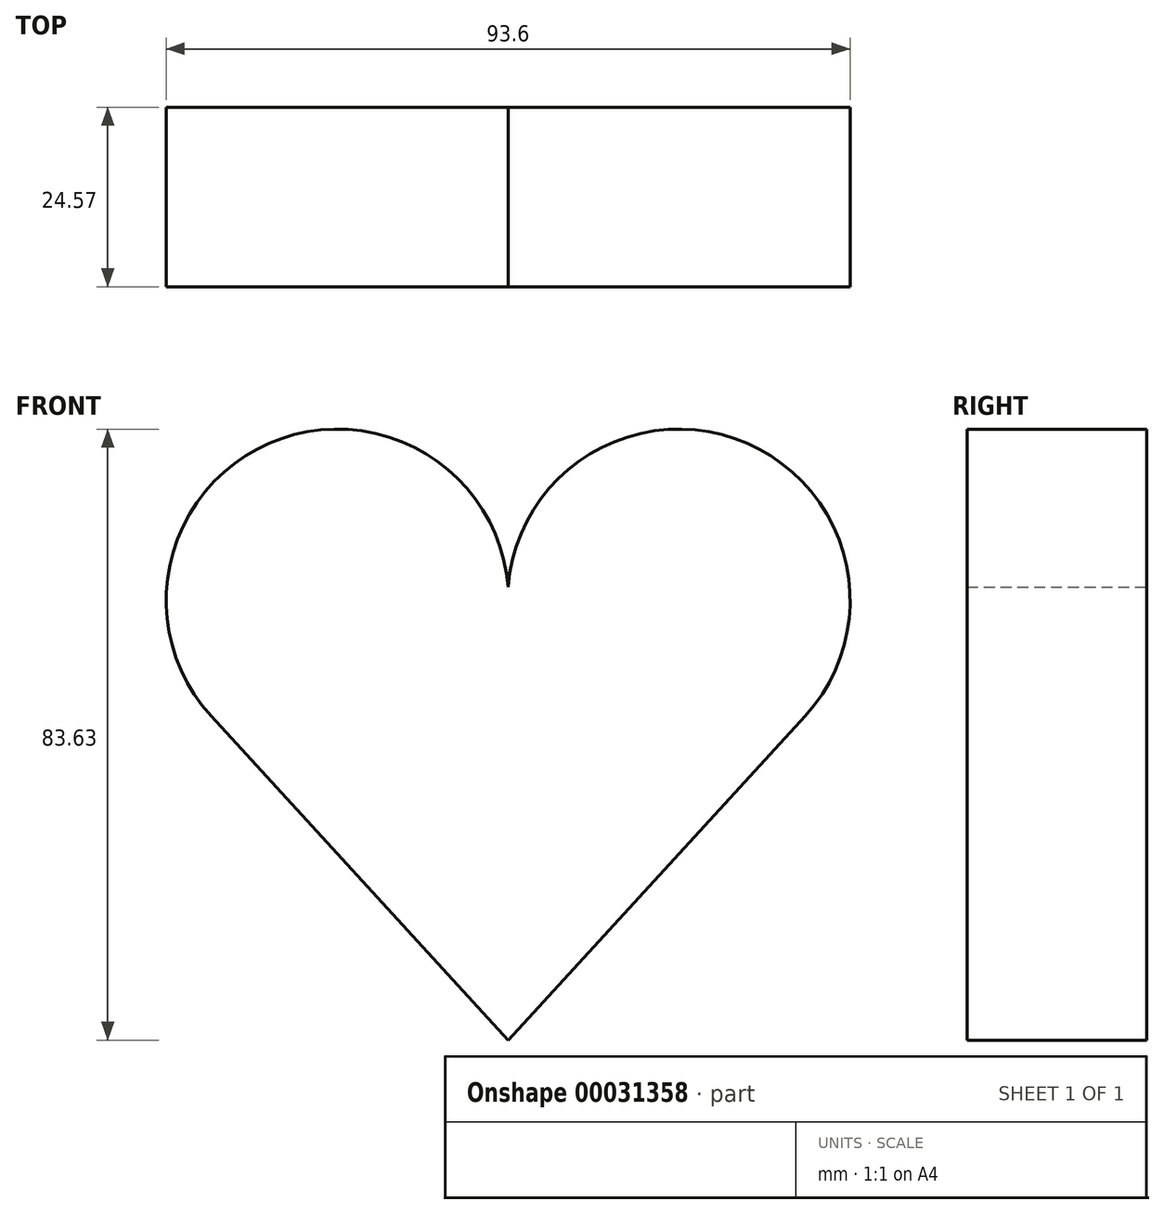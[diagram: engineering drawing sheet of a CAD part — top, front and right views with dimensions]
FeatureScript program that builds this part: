
annotation { "Feature Type Name" : "Feature", "Feature Type Description" : "" }
export const myFeature = defineFeature(function(context is Context, id is Id, definition is map)
    precondition{}
    {
        {
            var Q0;
            Q0=qCreatedBy(makeId("Front.planeOp"),FACE);
            var sketch = newSketch(context, id + "F0", { "sketchPlane" : qUnion([Q0])});
            skArc(sketch, "E0", {"start": v(40.64, 7.86) * mm, "mid": v(31, 45.85) * mm, "end": v(0, 21.86) * mm});
            skLineSegment(sketch, "E1", {"start": v(0, 25.53) * mm, "end": v(0, -36.5) * mm});
            skLineSegment(sketch, "E2", {"start": v(0, -36.5) * mm, "end": v(40.64, 7.86) * mm});
            skSolve(sketch);
        }
        {
            var Q0;
            {var subQ0=sQuery(id+"F0.wireOp",EDGE,"E2");Q0=makeQuery(id+"F0.imprint","IMPRINT",FACE,{"disambiguationData":[TD([[makeQuery(id+"F0.imprint","IMPRINT",EDGE,{"derivedFrom":subQ0}),1.0]])]});}
            extrude(context, id + "F1", {"entities" : qUnion([Q0]), "depth" : 24.57 * mm});
        }
        {
            var Q0;
            Q0=makeQuery(id+"F1.opExtrude","SWEPT_BODY",BODY,{"disambiguationData":[OSD([sQuery(id+"F0.wireOp",EDGE,"E0"),sQuery(id+"F0.wireOp",EDGE,"E1"),sQuery(id+"F0.wireOp",EDGE,"E2")])]});
            var Q1;
            Q1=qCreatedBy(makeId("Right.planeOp"),FACE);
            mirror(context, id + "F2", {"operationType" : NewBodyOperationType.ADD, "entities" : qUnion([Q0]), "mirrorPlane" : qUnion([Q1])});
        }
    });
